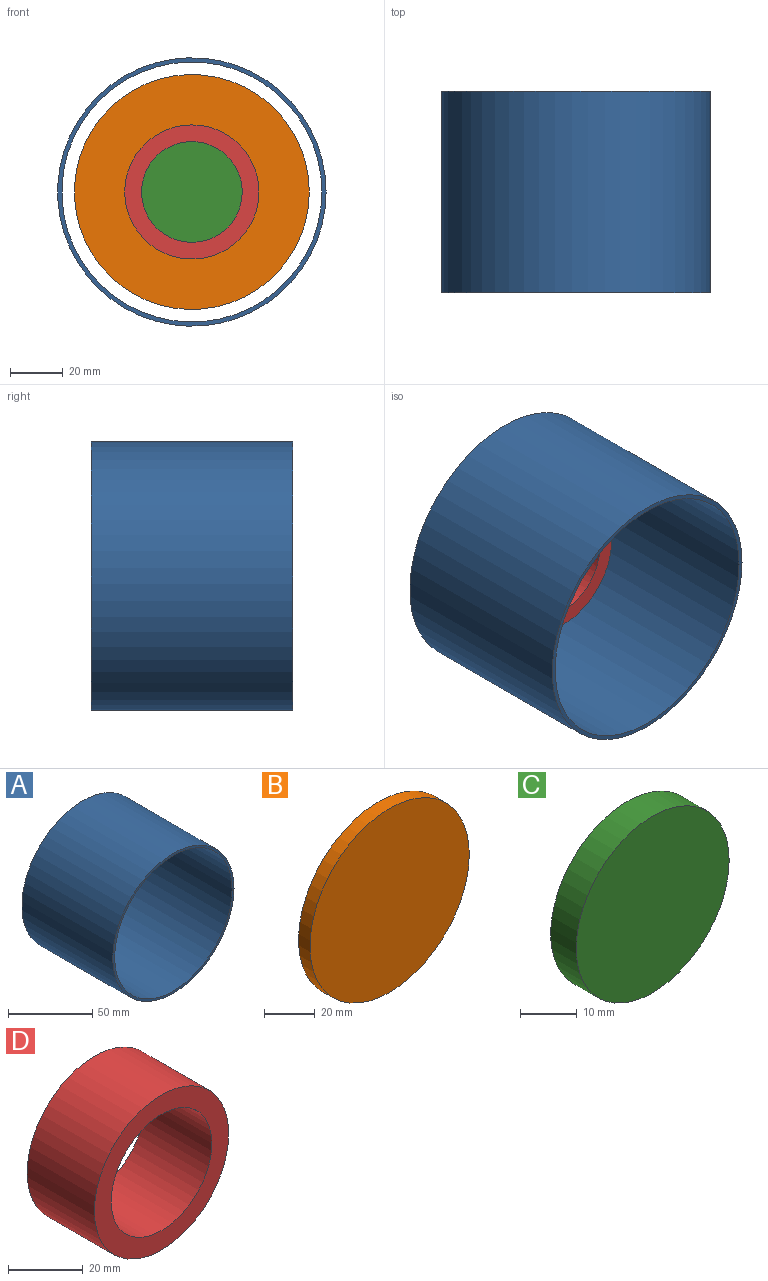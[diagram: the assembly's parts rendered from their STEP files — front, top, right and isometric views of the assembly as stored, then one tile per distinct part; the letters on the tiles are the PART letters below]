
ASSEMBLY  parts=4 mates=3
PART A: 4 faces, bbox 101.6x76.2x101.6 mm
  f0: cylinder r=49.21mm len=98.43mm, axis (0,1,0), area 23561.9mm2, adj f2,f3
  f1: cylinder r=50.8mm len=101.6mm, axis (0,1,0), area 24322mm2, adj f2,f3
  f2: plane 101.6x101.6mm, normal (0,-1,0), area 498.8mm2, adj f0,f1
  f3: plane 101.6x101.6mm, normal (0,1,0), area 498.8mm2, adj f0,f1
PART B: 3 faces, bbox 88.9x6.4x88.9 mm
  f0: cylinder r=44.45mm len=88.9mm, axis (0,1,0), area 1773.5mm2, adj f1,f2
  f1: plane 88.9x88.9mm, normal (0,-1,0), area 6207.2mm2, adj f0
  f2: plane 88.9x88.9mm, normal (0,1,0), area 6207.2mm2, adj f0
PART C: 3 faces, bbox 38.1x6.4x38.1 mm
  f0: cylinder r=19.05mm len=38.1mm, axis (0,1,0), area 760.1mm2, adj f1,f2
  f1: plane 38.1x38.1mm, normal (0,-1,0), area 1140.1mm2, adj f0
  f2: plane 38.1x38.1mm, normal (0,1,0), area 1140.1mm2, adj f0
PART D: 4 faces, bbox 50.8x25.4x50.8 mm
  f0: cylinder r=19.05mm len=38.1mm, axis (0,1,0), area 3040.2mm2, adj f2,f3
  f1: cylinder r=25.4mm len=50.8mm, axis (0,1,0), area 4053.7mm2, adj f2,f3
  f2: plane 50.8x50.8mm, normal (0,-1,0), area 886.7mm2, adj f0,f1
  f3: plane 50.8x50.8mm, normal (0,1,0), area 886.7mm2, adj f0,f1
PLACE A rot(axis=(0,1,0),0deg) t=(3.15,641.08,1540)mm
PLACE B rot(axis=(0,1,0),0deg) t=(3.15,641.08,1540)mm
PLACE C rot(axis=(0,-1,0),90deg) t=(3.15,634.73,1540)mm
PLACE D rot(axis=(0,-1,0),90deg) t=(3.15,634.73,1540)mm
MATE fastened A.f0 <-> B.f0  axis (0,1,0) through (3.15,641.08,1540)mm
MATE fastened D.f0 <-> C.f0  axis (0,1,0) through (3.15,634.73,1540)mm
MATE slider C.f0 <-> B.f0  axis (0,1,0) through (3.15,634.73,1540)mm
